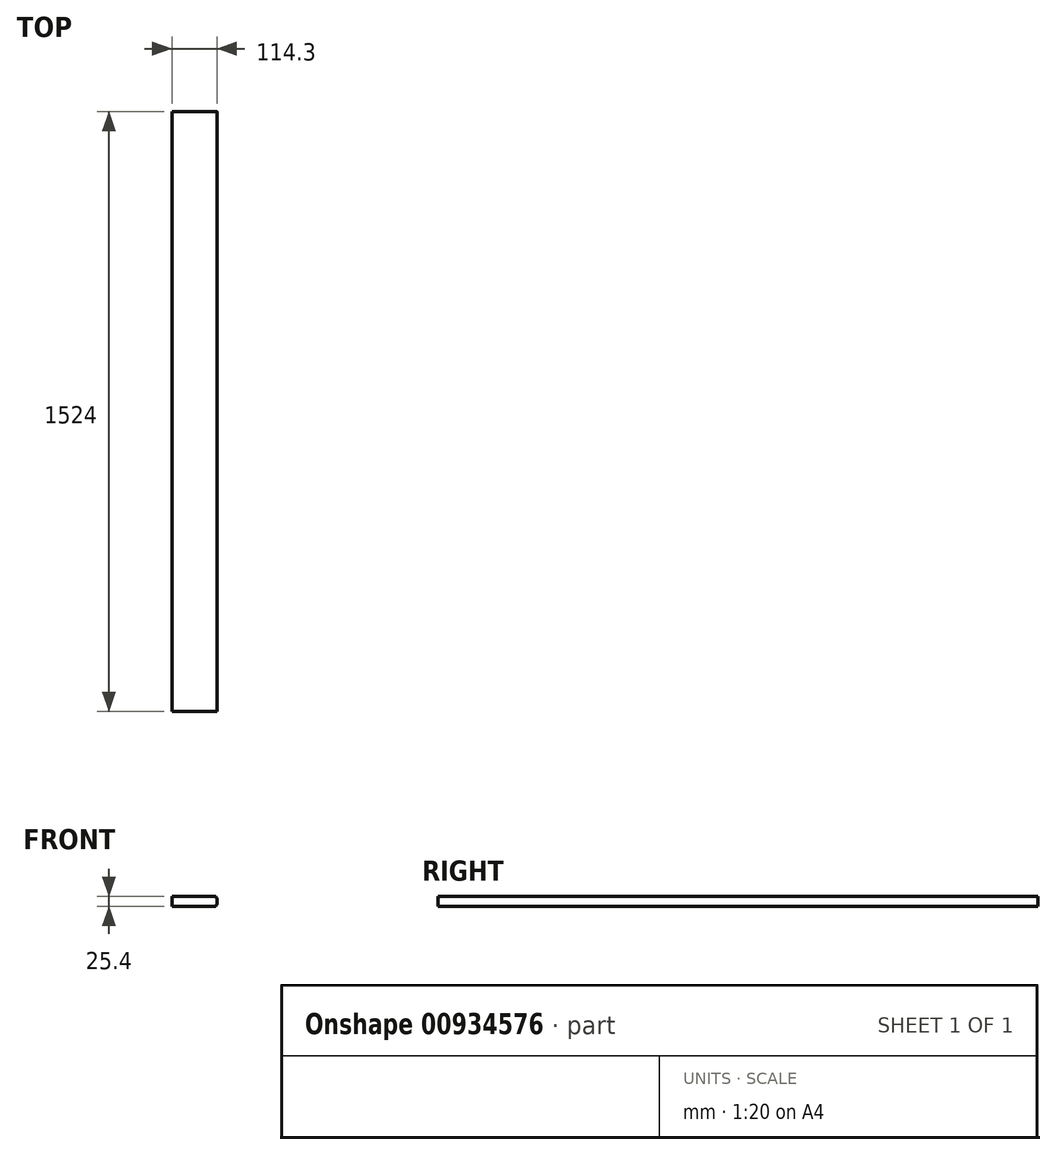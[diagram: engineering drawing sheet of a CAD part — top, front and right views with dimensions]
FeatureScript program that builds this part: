
annotation { "Feature Type Name" : "Feature", "Feature Type Description" : "" }
export const myFeature = defineFeature(function(context is Context, id is Id, definition is map)
    precondition{}
    {
        {
            var Q0;
            Q0=qCreatedBy(makeId("Front.planeOp"),FACE);
            var sketch = newSketch(context, id + "F0", { "sketchPlane" : qUnion([Q0])});
            skLineSegment(sketch, "E0.bottom", {"start": v(3577.98, 138.93) * mm, "end": v(3685.93, 138.93) * mm});
            skLineSegment(sketch, "E0.top", {"start": v(3577.98, 164.33) * mm, "end": v(3685.93, 164.33) * mm});
            skLineSegment(sketch, "E0.left", {"start": v(3577.98, 138.93) * mm, "end": v(3577.98, 164.33) * mm});
            skLineSegment(sketch, "E0.right", {"start": v(3692.28, 145.28) * mm, "end": v(3692.28, 157.98) * mm});
            skPoint(sketch, "E1.visualSharp", {"position": v(3692.28, 164.33) * mm});
            skArc(sketch, "E1.filletArc", {"start": v(3692.28, 157.98) * mm, "mid": v(3690.42, 162.47) * mm, "end": v(3685.93, 164.33) * mm});
            skPoint(sketch, "E2.visualSharp", {"position": v(3692.28, 138.93) * mm});
            skArc(sketch, "E2.filletArc", {"start": v(3685.93, 138.93) * mm, "mid": v(3690.42, 140.79) * mm, "end": v(3692.28, 145.28) * mm});
            skSolve(sketch);
        }
        {
            var Q0;
            Q0=makeQuery(id+"F0.imprint","IMPRINT",FACE,{"disambiguationData":[TD([[makeQuery(id+"F0.imprint","IMPRINT",EDGE,{"derivedFrom":sQuery(id+"F0.wireOp",EDGE,"E0.bottom")}),1.0]])]});
            extrude(context, id + "F1", {"entities" : qUnion([Q0]), "depth" : 1524 * mm, "offsetDistance" : 25.4 * mm});
        }
    });
